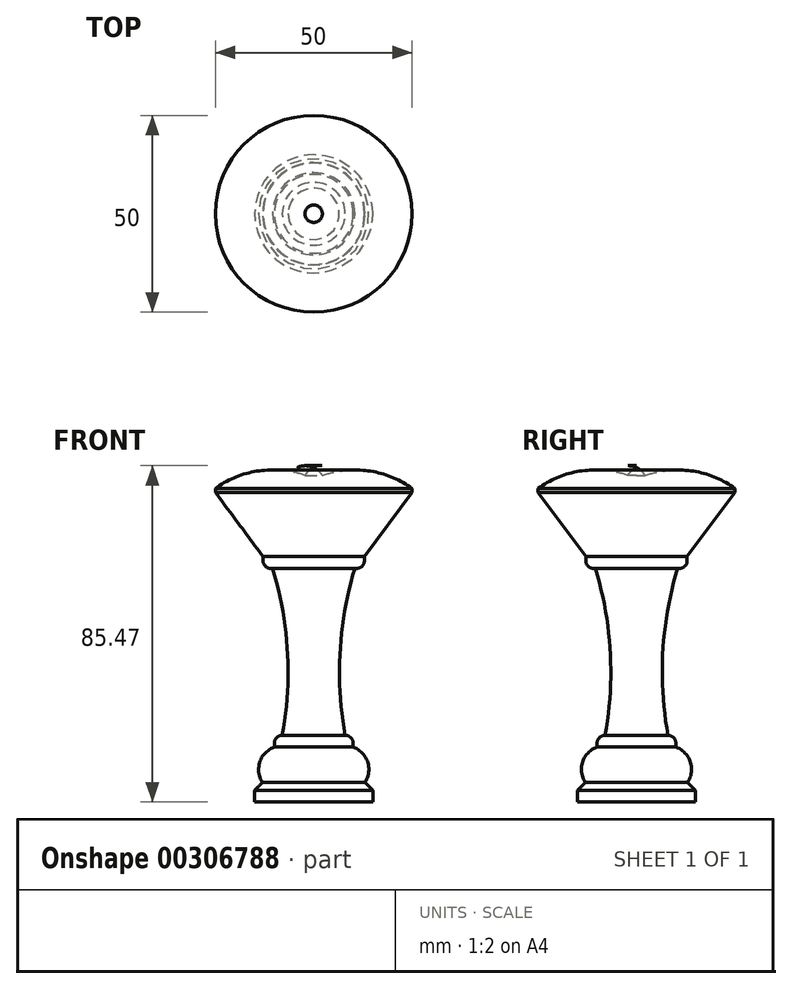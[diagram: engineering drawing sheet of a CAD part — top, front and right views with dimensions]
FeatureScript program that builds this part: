
annotation { "Feature Type Name" : "Feature", "Feature Type Description" : "" }
export const myFeature = defineFeature(function(context is Context, id is Id, definition is map)
    precondition{}
    {
        {
            var Q0;
            Q0=qCreatedBy(makeId("Front.planeOp"),FACE);
            var sketch = newSketch(context, id + "F0", { "sketchPlane" : qUnion([Q0])});
            skLineSegment(sketch, "E0", {"start": v(25, -5.27) * mm, "end": v(25, -6.27) * mm});
            skLineSegment(sketch, "E1", {"start": v(25, -6.27) * mm, "end": v(12.87, -22.65) * mm});
            skLineSegment(sketch, "E2", {"start": v(12.87, -22.65) * mm, "end": v(12.87, -23.65) * mm});
            skArc(sketch, "E3", {"start": v(10, -70.03) * mm, "mid": v(9.41, -68.62) * mm, "end": v(8, -68.03) * mm});
            skLineSegment(sketch, "E4", {"start": v(10, -70.03) * mm, "end": v(10, -71.03) * mm});
            skArc(sketch, "E5", {"start": v(13, -80) * mm, "mid": v(13.69, -74.78) * mm, "end": v(10, -71.03) * mm});
            skLineSegment(sketch, "E6", {"start": v(13, -80) * mm, "end": v(15, -82) * mm});
            skLineSegment(sketch, "E7", {"start": v(15, -82) * mm, "end": v(15, -85) * mm});
            skLineSegment(sketch, "E8", {"start": v(15, -85) * mm, "end": v(0, -85) * mm});
            skLineSegment(sketch, "E9", {"start": v(0, -85) * mm, "end": v(0, 0) * mm});
            skArc(sketch, "E10", {"start": v(25, -5.27) * mm, "mid": v(14, -0.85) * mm, "end": v(2.2, -2) * mm});
            skArc(sketch, "E11", {"start": v(10.45, -25.6) * mm, "mid": v(6.68, -46.67) * mm, "end": v(8, -68.03) * mm});
            skArc(sketch, "E12", {"start": v(10.45, -25.6) * mm, "mid": v(12.13, -25.2) * mm, "end": v(12.87, -23.65) * mm});
            skArc(sketch, "E13", {"start": v(2.2, -2) * mm, "mid": v(1.25, -0.83) * mm, "end": v(0, 0) * mm});
            skSolve(sketch);
        }
        {
            var Q0;
            Q0=makeQuery(id+"F0.imprint","IMPRINT",FACE,{"disambiguationData":[TD([[makeQuery(id+"F0.imprint","IMPRINT",EDGE,{"derivedFrom":sQuery(id+"F0.wireOp",EDGE,"E0")}),-1.0]])]});
            var Q1;
            Q1=sQuery(id+"F0.wireOp",EDGE,"E9");
            revolve(context, id + "F1", {"entities" : qUnion([Q0]), "axis" : qUnion([Q1]), "revolveType" : RevolveType.FULL});
        }
    });
